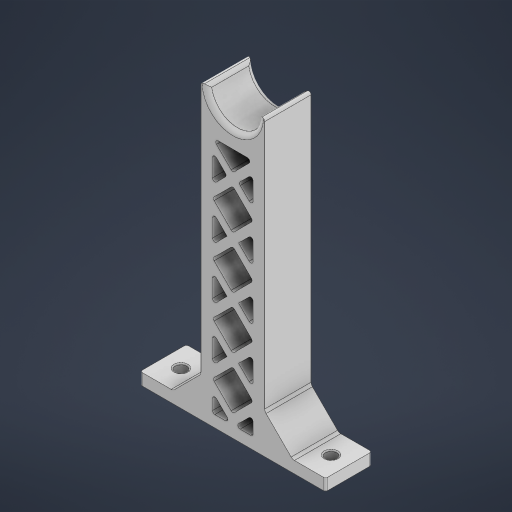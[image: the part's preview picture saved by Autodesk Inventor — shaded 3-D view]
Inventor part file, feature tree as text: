
AUTODESK INVENTOR PART (.ipt)
format: ipt  version: 2024.2 (Build 282272000, 272)  size: 449,024 bytes
history: native  units: mm
features: fillet x5, extrude x3, sketch x3, projected_geometry x2, chamfer x1
ambient origin geometry x8: Origin, YZ Plane, XZ Plane, XY Plane, X Axis, Y Axis, Z Axis, Center Point
bodies: Solid1 (feature_tree)
feature tree (14):
  extrude  "Extrusion1"  Depth=11.25mm
  fillet  "Fillet1"  Radius=11.25mm
  fillet  "Fillet2"  Radius=27.5mm
  chamfer  "Chamfer1"  Distance=5.0mm
  extrude  "Extrusion2"  Depth=20.0mm TaperAngle=0.0deg
  fillet  "Fillet3"  Radius=2.0mm
  fillet  "Fillet4"  Radius=1.0mm
  extrude  "Extrusion3"  Depth=2.0mm TaperAngle=45.0deg
  fillet  "Fillet5"  Radius=5.0mm
  sketch  "Sketch1"  dims[d0=115.0mm d1=22.5mm d2=11.25mm d3=27.5mm]
  sketch  "Sketch2"  dims[d4=40.0mm]
  projected_geometry  "Projected Loop1"
  projected_geometry  "Projected Loop2"
  sketch  "Sketch3"  dims[d5=40.0mm d6=5.0mm d7=20.0mm d8=0.0mm d9=2.0mm d10=1.0mm d11=12.0mm d12=2.0mm d13=45.0deg d14=5.0mm d15=5.0mm d16=10.0mm d17=7.625mm d18=14.25mm d19=7.625mm d20=7.625mm d21=10.0mm d22=20.0mm d23=0.0mm d24=0.5mm d25=2.0mm d26=0.0mm d27=5.0mm d28=5.0mm d29=5.0mm d30=45.0deg d31=5.0mm d32=5.0mm d33=45.0deg d34=5.0mm d35=5.0mm d36=5.0mm d37=5.0mm d38=45.0deg d39=5.0mm d40=5.0mm d41=20.0mm d42=0.0mm d43=1.0mm]
